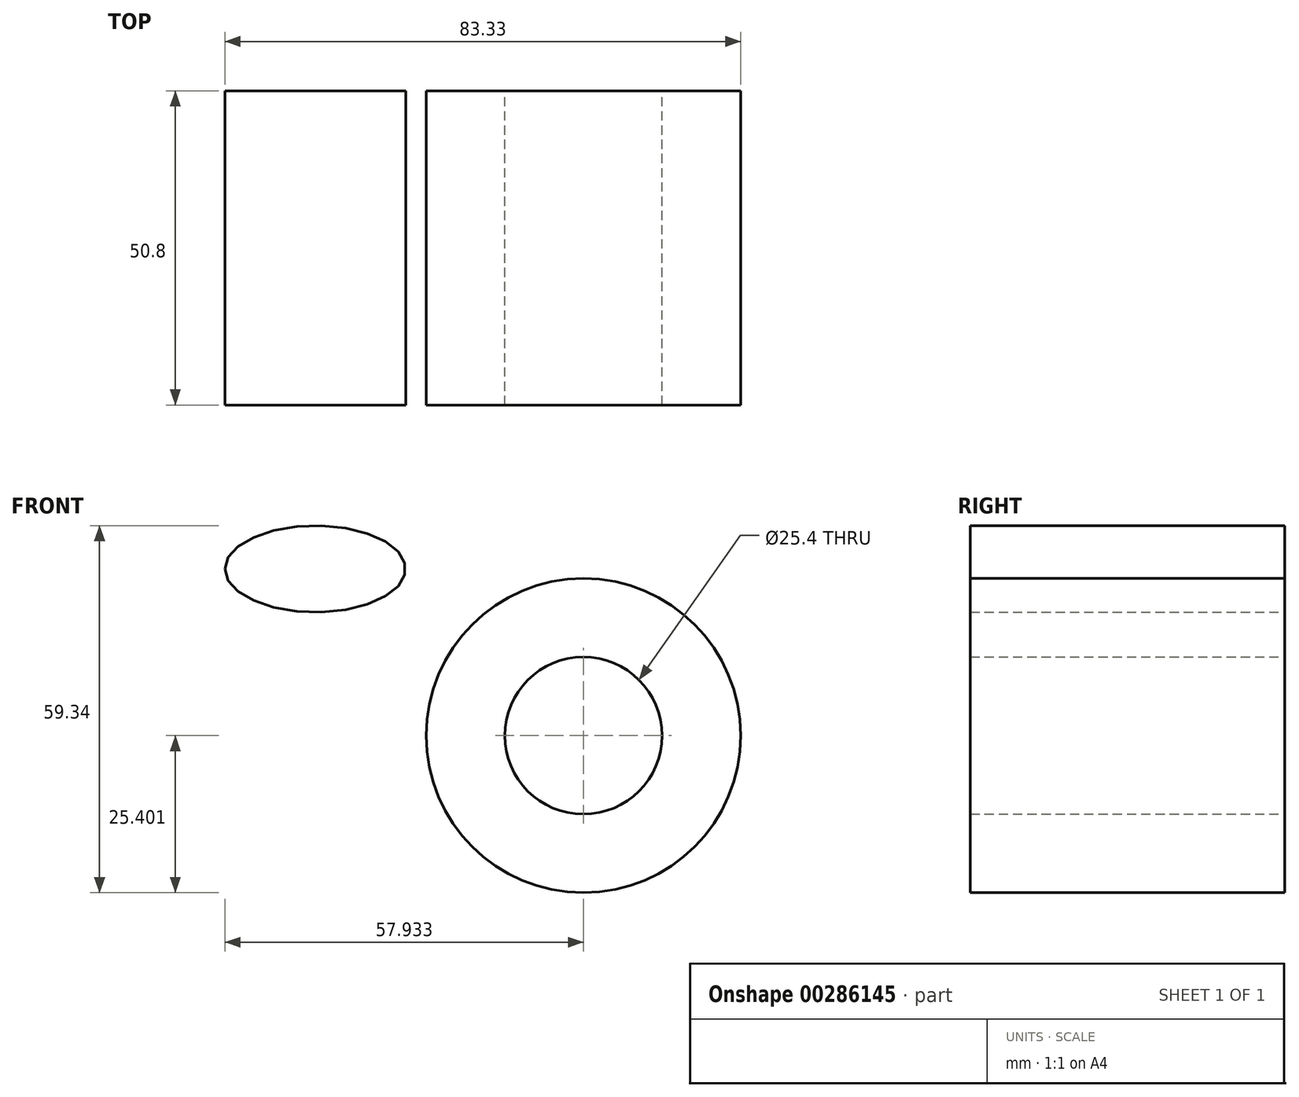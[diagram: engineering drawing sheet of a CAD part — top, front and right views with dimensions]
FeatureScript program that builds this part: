
annotation { "Feature Type Name" : "Feature", "Feature Type Description" : "" }
export const myFeature = defineFeature(function(context is Context, id is Id, definition is map)
    precondition{}
    {
        {
            var Q0;
            Q0=qCreatedBy(makeId("Front.planeOp"),FACE);
            var sketch = newSketch(context, id + "F0", { "sketchPlane" : qUnion([Q0])});
            skCircle(sketch, "E0", {"center": v(-121.07, 36.78) * mm, "radius": 25.4 * mm});
            skEllipse(sketch, "E1", {"center": v(-164.4, 63.73) * mm, "majorRadius": 14.6 * mm, "minorRadius": 6.99 * mm, "majorAxis": v(-1, 0)});
            skCircle(sketch, "E2", {"center": v(-121.07, 36.78) * mm, "radius": 12.7 * mm});
            skLineSegment(sketch, "E3.right", {"start": v(-50.62, 76.2) * mm, "end": v(-50.62, 0) * mm});
            skSolve(sketch);
        }
        {
            var Q0;
            Q0 = qSketchRegion(id + "F0", true);
            extrude(context, id + "F1", {"entities" : qUnion([Q0]), "depth" : 50.8 * mm});
        }
    });
